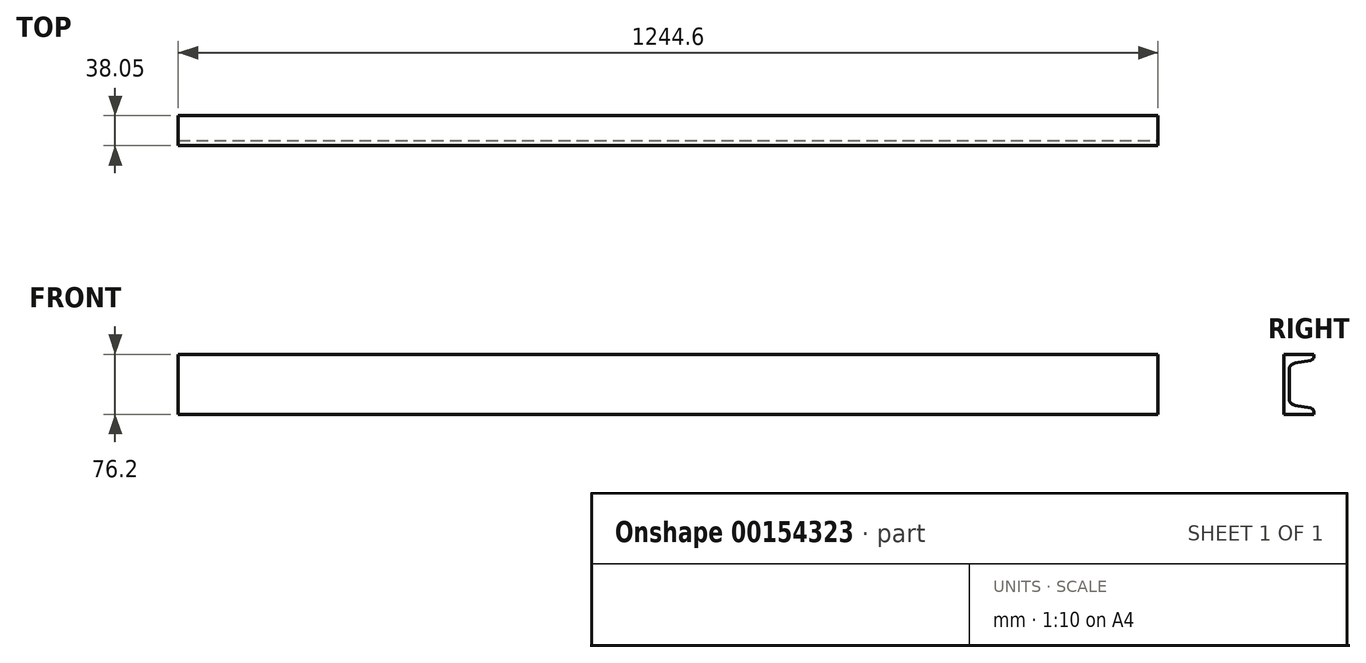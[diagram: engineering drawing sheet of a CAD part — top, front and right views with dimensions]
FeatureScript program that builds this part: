
annotation { "Feature Type Name" : "Feature", "Feature Type Description" : "" }
export const myFeature = defineFeature(function(context is Context, id is Id, definition is map)
    precondition{}
    {
        {
            var Q0;
            Q0=qCreatedBy(makeId("Right.planeOp"),FACE);
            var sketch = newSketch(context, id + "F0", { "sketchPlane" : qUnion([Q0])});
            skLineSegment(sketch, "E0", {"start": v(0, 0) * mm, "end": v(0, 76.2) * mm});
            skLineSegment(sketch, "E1", {"start": v(0, 0) * mm, "end": v(38.05, 0) * mm});
            skLineSegment(sketch, "E2", {"start": v(38.05, 0) * mm, "end": v(38.05, 6.93) * mm});
            skLineSegment(sketch, "E3", {"start": v(38.05, 6.93) * mm, "end": v(6.55, 12.7) * mm});
            skLineSegment(sketch, "E4", {"start": v(6.55, 12.7) * mm, "end": v(6.55, 63.5) * mm});
            skLineSegment(sketch, "E5", {"start": v(6.55, 63.5) * mm, "end": v(38.05, 69.27) * mm});
            skLineSegment(sketch, "E6", {"start": v(38.05, 69.27) * mm, "end": v(38.05, 76.2) * mm});
            skLineSegment(sketch, "E7", {"start": v(38.05, 76.2) * mm, "end": v(0, 76.2) * mm});
            skSolve(sketch);
        }
        {
            var Q0;
            Q0 = qSketchRegion(id + "F0", true);
            extrude(context, id + "F1", {"entities" : qUnion([Q0]), "oppositeDirection" : true, "depth" : 1244.6 * mm});
        }
        {
            var Q0;
            Q0=makeQuery(id+"F1.opExtrude","SWEPT_EDGE",EDGE,{"disambiguationData":[OSD([sQuery(id+"F0.wireOp",EDGE,"E5"),sQuery(id+"F0.wireOp",EDGE,"E6")])]});
            var Q1;
            Q1=makeQuery(id+"F1.opExtrude","SWEPT_EDGE",EDGE,{"disambiguationData":[OSD([sQuery(id+"F0.wireOp",EDGE,"E2"),sQuery(id+"F0.wireOp",EDGE,"E3")])]});
            fillet(context, id + "F2", {"entities" : qUnion([Q0, Q1]), "radius" : 5.08 * mm, "tangentPropagation" : true, "allowEdgeOverflow" : false});
        }
        {
            var Q0;
            Q0=makeQuery(id+"F1.opExtrude","SWEPT_EDGE",EDGE,{"disambiguationData":[OSD([sQuery(id+"F0.wireOp",EDGE,"E3"),sQuery(id+"F0.wireOp",EDGE,"E4")])]});
            var Q1;
            Q1=makeQuery(id+"F1.opExtrude","SWEPT_EDGE",EDGE,{"disambiguationData":[OSD([sQuery(id+"F0.wireOp",EDGE,"E4"),sQuery(id+"F0.wireOp",EDGE,"E5")])]});
            fillet(context, id + "F3", {"entities" : qUnion([Q0, Q1]), "radius" : 8.9 * mm, "tangentPropagation" : true, "allowEdgeOverflow" : false});
        }
    });
